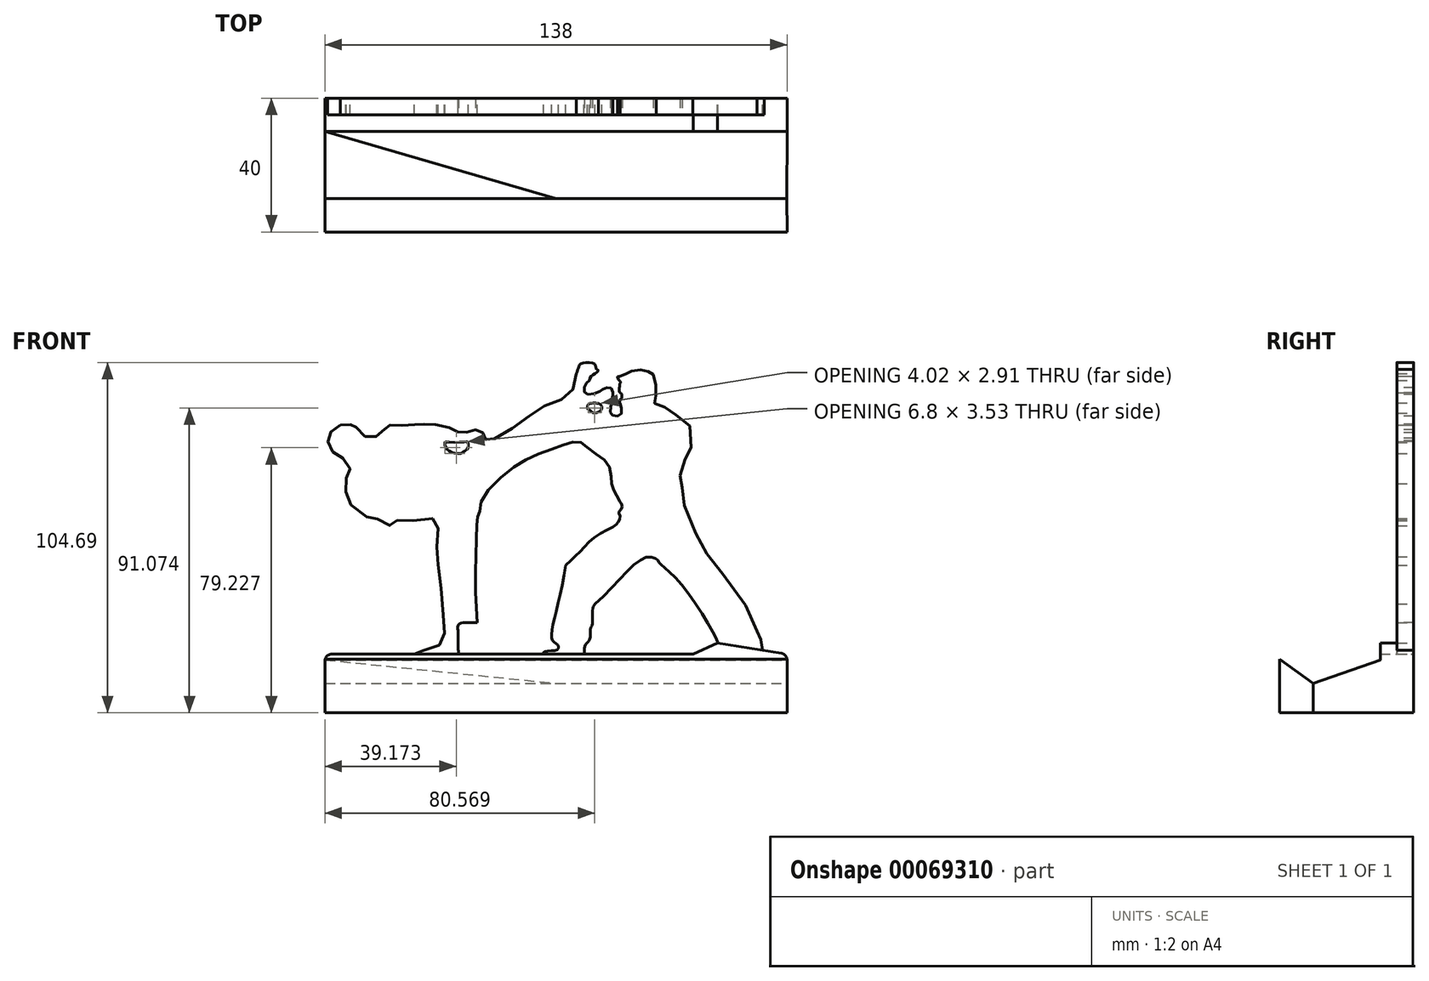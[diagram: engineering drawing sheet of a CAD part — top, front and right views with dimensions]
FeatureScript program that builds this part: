
annotation { "Feature Type Name" : "Feature", "Feature Type Description" : "" }
export const myFeature = defineFeature(function(context is Context, id is Id, definition is map)
    precondition{}
    {
        {
            var Q0;
            Q0=qCreatedBy(makeId("Front.planeOp"),FACE);
            var sketch = newSketch(context, id + "F0", { "sketchPlane" : qUnion([Q0])});
            skFitSpline(sketch, "E0", {"points": [v(4.6, 86.03) * mm, v(7.46, 86.1) * mm, v(7.84, 86.06) * mm, v(8.95, 85.67) * mm, v(11.96, 82.58) * mm, v(15.2, 82.46) * mm, v(17.79, 84.7) * mm, v(18.8, 85.9) * mm, v(20.85, 85.9) * mm, v(25.9, 86.05) * mm, v(28.33, 86.17) * mm, v(31.3, 86.29) * mm, v(35.56, 85.66) * mm, v(39.42, 84.26) * mm, v(39.87, 83.86) * mm, v(42.51, 83.84) * mm, v(44.68, 84.51) * mm, v(46.6, 84.3) * mm, v(47.46, 82.92) * mm, v(48.01, 81.62) * mm, v(49.31, 81.38) * mm, v(57.78, 86.34) * mm, v(65.86, 91.77) * mm, v(72.99, 95.11) * mm, v(75.02, 101.3) * mm], "startDerivative": vector(46.32, 15.6) * mm, "endDerivative": vector(14.2, 113.03) * mm});
            skFitSpline(sketch, "E1", {"points": [v(75.02, 101.3) * mm, v(75.7, 103.1) * mm, v(76.43, 104.3) * mm, v(80.47, 104.23) * mm, v(81, 102.77) * mm, v(81.66, 102.24) * mm, v(80.48, 101.3) * mm, v(78.94, 99.3) * mm], "startDerivative": vector(5.18, 13.6) * mm, "endDerivative": vector(-1.94, -17.12) * mm});
            skFitSpline(sketch, "E2", {"points": [v(78.94, 99.3) * mm, v(77.7, 97.78) * mm, v(77.81, 95.39) * mm, v(81.7, 95.83) * mm, v(83.48, 96.91) * mm, v(85.66, 96.84) * mm, v(85.41, 91.55) * mm, v(85.57, 89.1) * mm, v(88.31, 89.12) * mm, v(88.36, 91.74) * mm, v(88.07, 92.38) * mm, v(88.02, 93.51) * mm, v(88.48, 93.78) * mm, v(88.57, 95.38) * mm, v(88.13, 95.57) * mm], "startDerivative": vector(-19.58, -17.14) * mm, "endDerivative": vector(-19.03, -4.36) * mm});
            skFitSpline(sketch, "E3", {"points": [v(88.13, 95.57) * mm, v(87.99, 95.67) * mm, v(88.02, 98.16) * mm, v(88.13, 98.46) * mm, v(88.29, 98.67) * mm, v(87.7, 99.56) * mm, v(87.38, 100.44) * mm, v(88.13, 100.53) * mm], "startDerivative": vector(-2.17, 0.23) * mm, "endDerivative": vector(5.55, 3.7) * mm});
            skFitSpline(sketch, "E4", {"points": [v(88.13, 100.53) * mm, v(88.7, 100.85) * mm, v(88.82, 101.1) * mm, v(90, 101.36) * mm, v(90.38, 101.87) * mm, v(91.33, 102.01) * mm, v(92.59, 102.44) * mm, v(94.2, 102.54) * mm, v(95.82, 102.06) * mm, v(96.33, 101.97) * mm, v(97.12, 101.8) * mm, v(97.42, 101.28) * mm, v(98.05, 101.08) * mm, v(98.65, 99.31) * mm, v(98.8, 96.48) * mm, v(98.8, 94.82) * mm, v(98.3, 94.5) * mm, v(98.34, 92.58) * mm, v(100.07, 91.95) * mm, v(102.4, 90.65) * mm, v(105.35, 88.6) * mm, v(109.56, 84.35) * mm, v(108.46, 76.83) * mm, v(107.46, 75.77) * mm, v(106, 70.43) * mm, v(106.57, 67.8) * mm, v(106.8, 64.28) * mm, v(112.15, 50.58) * mm, v(116.89, 43.9) * mm, v(128.89, 25.53) * mm, v(129.18, 22.46) * mm, v(130.77, 21.4) * mm, v(130.8, 18.82) * mm, v(126.06, 19.22) * mm, v(117.95, 20.11) * mm, v(117.16, 21.34) * mm, v(105.9, 39.04) * mm, v(99.9, 44.8) * mm, v(99.23, 45.74) * mm, v(95.59, 46.33) * mm, v(80.69, 32.5) * mm], "startDerivative": vector(65.24, 25.4) * mm, "endDerivative": vector(-279.7, -241.57) * mm});
            skFitSpline(sketch, "E5", {"points": [v(80.69, 32.5) * mm, v(79.96, 31.17) * mm, v(79.76, 26.2) * mm, v(79.3, 25.2) * mm, v(79.03, 21.9) * mm, v(77.64, 19.96) * mm, v(76.47, 16.23) * mm, v(65.9, 16.9) * mm, v(65.45, 18.19) * mm, v(69.36, 18.85) * mm, v(69.5, 20.3) * mm, v(67.9, 21.63) * mm, v(71.89, 44.02) * mm], "startDerivative": vector(-17.32, -17.7) * mm, "endDerivative": vector(25.35, 168.99) * mm});
            skFitSpline(sketch, "E6", {"points": [v(71.89, 44.02) * mm, v(76.38, 48.43) * mm, v(81.07, 52.83) * mm, v(86.68, 55.92) * mm, v(87.5, 57.02) * mm, v(88.12, 58.54) * mm, v(87.74, 59.78) * mm, v(87.92, 60.18) * mm, v(88.43, 60.76) * mm, v(88.7, 62.18) * mm, v(88.02, 63.2) * mm, v(87.62, 63.86) * mm, v(85.63, 68.45) * mm], "startDerivative": vector(36.48, 34.37) * mm, "endDerivative": vector(-9.12, 41.25) * mm});
            skFitSpline(sketch, "E7", {"points": [v(85.63, 68.45) * mm, v(85.4, 70.7) * mm, v(84.68, 74.1) * mm, v(82.17, 76.5) * mm, v(78.17, 79.34) * mm, v(76.36, 80.86) * mm, v(73.53, 80.82) * mm, v(68.78, 79.13) * mm, v(61.46, 76.33) * mm, v(54.3, 71.78) * mm, v(46.9, 63.68) * mm, v(46.2, 60.12) * mm, v(45.7, 58.7) * mm, v(45.33, 56.48) * mm, v(45.06, 46.9) * mm, v(45.47, 26.92) * mm], "startDerivative": vector(-4.63, 45.54) * mm, "endDerivative": vector(16.83, -257.46) * mm});
            skFitSpline(sketch, "E8", {"points": [v(45.47, 26.92) * mm, v(39.96, 26.45) * mm, v(39.73, 24.16) * mm, v(39.82, 18.17) * mm, v(39.69, 17.47) * mm, v(34.45, 17.2) * mm, v(27.48, 17.16) * mm, v(26.81, 17) * mm, v(26.81, 17.94) * mm, v(28.2, 18.44) * mm, v(33.66, 19.94) * mm, v(35.56, 22.73) * mm, v(35.44, 27.9) * mm, v(34.15, 41.54) * mm, v(33.43, 48.44) * mm, v(33.71, 55.28) * mm, v(32.77, 57.9) * mm, v(26.03, 57.43) * mm, v(21.44, 57.43) * mm, v(20.04, 55.93) * mm, v(17.88, 56.77) * mm, v(14.23, 58.27) * mm, v(12.36, 58.55) * mm, v(6.68, 63.57) * mm, v(6.3, 66.57) * mm, v(6.4, 70.31) * mm, v(7.33, 72.28) * mm, v(7.14, 73.97) * mm, v(4.15, 76.87) * mm, v(2.27, 78) * mm, v(1, 80.23) * mm, v(0.9, 82.55) * mm, v(2.27, 84.4) * mm, v(4.6, 86.03) * mm], "startDerivative": vector(-187.96, 6.71) * mm, "endDerivative": vector(76.8, 54.04) * mm});
            skFitSpline(sketch, "E9", {"points": [v(36.2, 80.95) * mm, v(42.04, 81) * mm, v(42.52, 80.97) * mm, v(42.63, 79) * mm, v(41.28, 78) * mm, v(40.82, 77.57) * mm, v(38.3, 77.64) * mm, v(36.35, 78.9) * mm, v(35.76, 80.42) * mm, v(36, 81.03) * mm, v(36.2, 80.95) * mm]});
            skFitSpline(sketch, "E10", {"points": [v(80.15, 92.53) * mm, v(81.7, 92.45) * mm, v(82.45, 91.96) * mm, v(82.59, 90.82) * mm, v(81.7, 89.87) * mm, v(79.9, 89.71) * mm, v(79.14, 90.4) * mm, v(78.53, 90.66) * mm, v(78.63, 92.14) * mm, v(80.15, 92.53) * mm]});
            skSolve(sketch);
        }
        {
            var Q0;
            Q0=makeQuery(id+"F0.imprint","IMPRINT",FACE,{"disambiguationData":[TD([[makeQuery(id+"F0.imprint","IMPRINT",EDGE,{"derivedFrom":sQuery(id+"F0.wireOp",EDGE,"E0")}),-1.0]])]});
            extrude(context, id + "F1", {"entities" : qUnion([Q0]), "depth" : 5 * mm});
        }
        {
            var Q0;
            Q0=qCreatedBy(makeId("Front.planeOp"),FACE);
            var sketch = newSketch(context, id + "F2", { "sketchPlane" : qUnion([Q0])});
            skLineSegment(sketch, "E11", {"start": v(0, 0) * mm, "end": v(0, 17.5) * mm});
            skLineSegment(sketch, "E12", {"start": v(0, 17.5) * mm, "end": v(110, 17.5) * mm});
            skLineSegment(sketch, "E13", {"start": v(110, 17.5) * mm, "end": v(117.25, 20.88) * mm});
            skLineSegment(sketch, "E14", {"start": v(117.25, 20.88) * mm, "end": v(137.98, 17.5) * mm});
            skLineSegment(sketch, "E15", {"start": v(137.98, 17.5) * mm, "end": v(137.98, 0) * mm});
            skLineSegment(sketch, "E16", {"start": v(137.98, 0) * mm, "end": v(0, 0) * mm});
            skSolve(sketch);
        }
        {
            var Q0;
            Q0 = qSketchRegion(id + "F2", true);
            extrude(context, id + "F3", {"entities" : qUnion([Q0]), "operationType" : NewBodyOperationType.ADD, "depth" : 10 * mm});
        }
        {
            var Q0;
            Q0=makeQuery(id+"F3.opExtrude","CAP_FACE",FACE,{"disambiguationData":[OSD([sQuery(id+"F2.wireOp",EDGE,"E11"),sQuery(id+"F2.wireOp",EDGE,"E12"),sQuery(id+"F2.wireOp",EDGE,"E13"),sQuery(id+"F2.wireOp",EDGE,"E14"),sQuery(id+"F2.wireOp",EDGE,"E15"),sQuery(id+"F2.wireOp",EDGE,"E16")])],"isStart":false});
            var sketch = newSketch(context, id + "F4", { "sketchPlane" : qUnion([Q0])});
            skLineSegment(sketch, "E17", {"start": v(0, 0) * mm, "end": v(0, 8.75) * mm});
            skLineSegment(sketch, "E18", {"start": v(0, 8.75) * mm, "end": v(137.98, 8.75) * mm});
            skLineSegment(sketch, "E19", {"start": v(137.98, 8.75) * mm, "end": v(137.98, 0) * mm});
            skLineSegment(sketch, "E20", {"start": v(137.98, 0) * mm, "end": v(0, 0) * mm});
            skSolve(sketch);
        }
        {
            var Q0;
            Q0 = qSketchRegion(id + "F4", true);
            extrude(context, id + "F5", {"entities" : qUnion([Q0]), "depth" : 40 * mm});
        }
        {
            var Q0;
            Q0=makeQuery(id+"F5.opExtrude","CAP_FACE",FACE,{"disambiguationData":[OSD([sQuery(id+"F4.wireOp",EDGE,"E17"),sQuery(id+"F4.wireOp",EDGE,"E18"),sQuery(id+"F4.wireOp",EDGE,"E19"),sQuery(id+"F4.wireOp",EDGE,"E20")])],"isStart":false});
            var sketch = newSketch(context, id + "F6", { "sketchPlane" : qUnion([Q0])});
            skLineSegment(sketch, "E21", {"start": v(0, 15) * mm, "end": v(137.98, 15) * mm});
            skLineSegment(sketch, "E22", {"start": v(137.98, 15) * mm, "end": v(137.98, 0) * mm});
            skLineSegment(sketch, "E23", {"start": v(137.98, 0) * mm, "end": v(0, 0) * mm});
            skLineSegment(sketch, "E24", {"start": v(0, 15) * mm, "end": v(0, 0) * mm});
            skSolve(sketch);
        }
        {
            var Q0;
            {var subQ0=sQuery(id+"F6.wireOp",EDGE,"E21");Q0=makeQuery(id+"F6.imprint","IMPRINT",FACE,{"disambiguationData":[TD([[makeQuery(id+"F6.imprint","IMPRINT",EDGE,{"derivedFrom":subQ0}),-1.0]])]});}
            var Q1;
            {var subQ0=sQuery(id+"F6.wireOp",EDGE,"E23");Q1=makeQuery(id+"F6.imprint","IMPRINT",FACE,{"disambiguationData":[TD([[makeQuery(id+"F6.imprint","IMPRINT",EDGE,{"derivedFrom":subQ0}),-1.0]])]});}
            extrude(context, id + "F7", {"entities" : qUnion([Q0, Q1]), "operationType" : NewBodyOperationType.ADD, "depth" : 5 * mm});
        }
        {
            var Q0;
            Q0=makeQuery(id+"F5.opExtrude","SWEPT_EDGE",EDGE,{"disambiguationData":[OSD([sQuery(id+"F2.wireOp",EDGE,"E15"),sQuery(id+"F4.wireOp",EDGE,"E18"),sQuery(id+"F4.wireOp",EDGE,"E19")])]});
            var Q1;
            Q1=makeQuery(id+"F5.opExtrude","SWEPT_EDGE",EDGE,{"disambiguationData":[OSD([sQuery(id+"F2.wireOp",EDGE,"E11"),sQuery(id+"F4.wireOp",EDGE,"E17"),sQuery(id+"F4.wireOp",EDGE,"E18")])]});
            var Q2;
            Q2=makeQuery(id+"F7.opExtrude","CAP_EDGE",EDGE,{"disambiguationData":[OSD([sQuery(id+"F6.wireOp",EDGE,"E22")])],"isStart":false});
            var Q3;
            Q3=makeQuery(id+"F7.opExtrude","CAP_EDGE",EDGE,{"disambiguationData":[OSD([sQuery(id+"F6.wireOp",EDGE,"E24")])],"isStart":false});
            var Q4;
            Q4=makeQuery(id+"F7.opExtrude","CAP_EDGE",EDGE,{"disambiguationData":[OSD([sQuery(id+"F6.wireOp",EDGE,"E21")])],"isStart":true});
            var Q5;
            Q5=makeQuery(id+"F7.opExtrude","CAP_EDGE",EDGE,{"disambiguationData":[OSD([sQuery(id+"F6.wireOp",EDGE,"E22")])],"isStart":true});
            var Q6;
            Q6=makeQuery(id+"F7.opExtrude","CAP_EDGE",EDGE,{"disambiguationData":[OSD([sQuery(id+"F6.wireOp",EDGE,"E24")])],"isStart":true});
            var Q7;
            Q7=makeQuery(id+"F3.opExtrude","SWEPT_EDGE",EDGE,{"disambiguationData":[OSD([sQuery(id+"F2.wireOp",EDGE,"E11"),sQuery(id+"F2.wireOp",EDGE,"E12")])]});
            var Q8;
            Q8=makeQuery(id+"F3.opExtrude","SWEPT_EDGE",EDGE,{"disambiguationData":[OSD([sQuery(id+"F2.wireOp",EDGE,"E14"),sQuery(id+"F2.wireOp",EDGE,"E15")])]});
            fillet(context, id + "F8", {"entities" : qUnion([Q0, Q1, Q2, Q3, Q4, Q5, Q6, Q7, Q8]), "radius" : 2 * mm, "tangentPropagation" : true, "allowEdgeOverflow" : false});
        }
        {
            var Q0;
            Q0=makeQuery(id+"F5.opExtrude","SWEPT_BODY",BODY,{"disambiguationData":[OSD([sQuery(id+"F4.wireOp",EDGE,"E17"),sQuery(id+"F4.wireOp",EDGE,"E18"),sQuery(id+"F4.wireOp",EDGE,"E19"),sQuery(id+"F4.wireOp",EDGE,"E20")])]});
            deleteBodies(context, id + "F9", {"entities" : qUnion([Q0])});
        }
        {
            var Q0;
            Q0=makeQuery(id+"F3.opExtrude","CAP_FACE",FACE,{"disambiguationData":[OSD([sQuery(id+"F2.wireOp",EDGE,"E11"),sQuery(id+"F2.wireOp",EDGE,"E12"),sQuery(id+"F2.wireOp",EDGE,"E13"),sQuery(id+"F2.wireOp",EDGE,"E14"),sQuery(id+"F2.wireOp",EDGE,"E15"),sQuery(id+"F2.wireOp",EDGE,"E16")])],"isStart":false});
            cPlane(context, id + "F10", {"entities" : qUnion([Q0]), "cplaneType" : CPlaneType.OFFSET, "offset" : 20 * mm, "width" : 150 * mm, "height" : 150 * mm});
        }
        {
            var Q0;
            Q0=qCreatedBy(id+"F10.planeOp",FACE);
            var sketch = newSketch(context, id + "F11", { "sketchPlane" : qUnion([Q0])});
            skLineSegment(sketch, "E25.bottom", {"start": v(0, 0) * mm, "end": v(137.86, 0) * mm});
            skLineSegment(sketch, "E25.top", {"start": v(0, 8.76) * mm, "end": v(137.86, 8.76) * mm});
            skLineSegment(sketch, "E25.left", {"start": v(0, 0) * mm, "end": v(0, 8.76) * mm});
            skLineSegment(sketch, "E25.right", {"start": v(137.86, 0) * mm, "end": v(137.86, 8.76) * mm});
            skSolve(sketch);
        }
        {
            var Q0;
            Q0=makeQuery(id+"F3.opExtrude","CAP_FACE",FACE,{"disambiguationData":[OSD([sQuery(id+"F2.wireOp",EDGE,"E11"),sQuery(id+"F2.wireOp",EDGE,"E12"),sQuery(id+"F2.wireOp",EDGE,"E13"),sQuery(id+"F2.wireOp",EDGE,"E14"),sQuery(id+"F2.wireOp",EDGE,"E15"),sQuery(id+"F2.wireOp",EDGE,"E16")])],"isStart":false});
            var sketch = newSketch(context, id + "F12", { "sketchPlane" : qUnion([Q0])});
            skLineSegment(sketch, "E26.bottom", {"start": v(0, 0) * mm, "end": v(137.98, 0) * mm});
            skLineSegment(sketch, "E26.top", {"start": v(0, 15.8) * mm, "end": v(137.98, 15.8) * mm});
            skLineSegment(sketch, "E26.left", {"start": v(0, 0) * mm, "end": v(0, 15.8) * mm});
            skLineSegment(sketch, "E26.right", {"start": v(137.98, 0) * mm, "end": v(137.98, 15.8) * mm});
            skSolve(sketch);
        }
        {
            var Q1;
            {var subQ1=sQuery(id+"F12.wireOp",EDGE,"E26.bottom");Q1=makeQuery(id+"F12.imprint","IMPRINT",FACE,{"disambiguationData":[TD([[makeQuery(id+"F12.imprint","IMPRINT",EDGE,{"derivedFrom":subQ1}),-1.0]])]});}
            var Q2;
            Q2=makeQuery(id+"F11.imprint","IMPRINT",FACE,{"disambiguationData":[TD([[makeQuery(id+"F11.imprint","IMPRINT",EDGE,{"derivedFrom":sQuery(id+"F11.wireOp",EDGE,"E25.bottom")}),1.0]])]});
            var Q3;
            Q3=sQuery(id+"F12.wireOp",VERTEX,"E26.right.end");
            var Q4;
            Q4=sQuery(id+"F11.wireOp",VERTEX,"E25.right.end");
            loft(context, id + "F13", {"operationType" : NewBodyOperationType.ADD, "sheetProfilesArray" : [{ "sheetProfileEntities" : qUnion([Q1]) }, { "sheetProfileEntities" : qUnion([Q2]) }], "matchConnections" : true, "connections" : [{ "connectionEntities" : qUnion([Q3, Q4]), "connectionEdgeQueries" : qUnion([]), "connectionEdgeParameters" : [] }]});
        }
        {
            var Q0;
            Q0=makeQuery(id+"F13.opLoft","CAP_FACE",FACE,{"disambiguationData":[OSD([makeQuery(id+"F11.imprint","IMPRINT",FACE,{"disambiguationData":[TD([[makeQuery(id+"F11.imprint","IMPRINT",EDGE,{"derivedFrom":sQuery(id+"F11.wireOp",EDGE,"E25.bottom")}),1.0]])]})])],"isStart":true});
            cPlane(context, id + "F14", {"entities" : qUnion([Q0]), "cplaneType" : CPlaneType.OFFSET, "offset" : 10 * mm, "width" : 150 * mm, "height" : 150 * mm});
        }
        {
            var Q0;
            Q0=qCreatedBy(id+"F14.planeOp",FACE);
            var sketch = newSketch(context, id + "F15", { "sketchPlane" : qUnion([Q0])});
            skLineSegment(sketch, "E27.bottom", {"start": v(0, 0) * mm, "end": v(138, 0) * mm});
            skLineSegment(sketch, "E27.top", {"start": v(0, 16) * mm, "end": v(138, 16) * mm});
            skLineSegment(sketch, "E27.left", {"start": v(0, 0) * mm, "end": v(0, 16) * mm});
            skLineSegment(sketch, "E27.right", {"start": v(138, 0) * mm, "end": v(138, 16) * mm});
            skSolve(sketch);
        }
        {
            var Q1;
            Q1=makeQuery(id+"F13.opLoft","CAP_FACE",FACE,{"disambiguationData":[OSD([makeQuery(id+"F11.imprint","IMPRINT",FACE,{"disambiguationData":[TD([[makeQuery(id+"F11.imprint","IMPRINT",EDGE,{"derivedFrom":sQuery(id+"F11.wireOp",EDGE,"E25.bottom")}),1.0]])]})])],"isStart":true});
            var Q2;
            Q2=makeQuery(id+"F15.imprint","IMPRINT",FACE,{"disambiguationData":[TD([[makeQuery(id+"F15.imprint","IMPRINT",EDGE,{"derivedFrom":sQuery(id+"F15.wireOp",EDGE,"E27.bottom")}),1.0]])]});
            var Q3;
            Q3=makeQuery(id+"F13.opLoft","MID_CAP_VERTEX",VERTEX,{"disambiguationData":[OSD([sQuery(id+"F11.wireOp",EDGE,"E25.top"),sQuery(id+"F11.wireOp",EDGE,"E25.right")])],"capPos":1.0});
            var Q4;
            Q4=sQuery(id+"F15.wireOp",VERTEX,"E27.top.end");
            loft(context, id + "F16", {"operationType" : NewBodyOperationType.ADD, "sheetProfilesArray" : [{ "sheetProfileEntities" : qUnion([Q1]) }, { "sheetProfileEntities" : qUnion([Q2]) }], "matchConnections" : true, "connections" : [{ "connectionEntities" : qUnion([Q3, Q4]), "connectionEdgeQueries" : qUnion([]), "connectionEdgeParameters" : [] }]});
        }
    });
